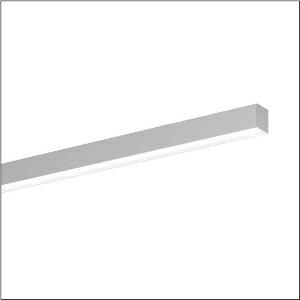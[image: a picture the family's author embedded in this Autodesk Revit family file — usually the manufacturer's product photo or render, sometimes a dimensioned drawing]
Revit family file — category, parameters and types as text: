
# Revit family: silica_r__21_51mx23tbt5s_3fb0
name_source: partatom
category: Lighting Fixtures
units: mm (PartAtom-declared; Revit-internal decimal feet)

## family parameters
Cut with Voids When Loaded = No
Host = Face
Light Source = No
Part Type = Normal
Room Calculation Point = No
Round Connector Dimension = Use Diameter
Shared = No

## types (1)
- --- (1 x LED, 4030 lm, 40.5 W, 6500K)
    Apparent Load = 41 VA
    CIE Flux Codes = 78 96 99 100 100
    Color Rendering = 80
    Color Temperature = 6500K
    Default Elevation = 1800 mm
    Description = Silica® 21, office luminaire, primary optical cover: prismatic diffuser, of PMMA, CAT 2 (L<= 3000cd/m²), light emission: direct distribution, primary light characteristic: symmetric, installation type: surface-mounted, LED, rated luminous flux: 4.030lm, luminous efficacy: 95lm/W, light colour: 8tw, colour temperature: 2700..6500K, control gear: ECG DALI, with terminal, 3+2-pole, max. 2.5mm², mains connection: 220..240V, AC, 50/60Hz, rated input power: 42.6W, luminaire housing, of aluminium, metallic grey (RAL 9006), length: 1.504mm, width: 53mm, height: 53mm, protection rating (complete): IP20, insulation class (complete): insulation class I (protective earthing), certification: CE, permissible operating ambient temperature: 0..+35°C, standard: EN 50419, packaging unit: 1 piece
    Height = 0 mm  [stored 0 ft]
    Lamp = 1 x LED
    Lamp Light Flux = 4030 lm
    Lamp Power = 40.5 W
    Lamp count = 1
    Length = 1504 mm
    Luminous efficacy = 100 lm/W
    Manufacturer = Siteco
    ModVariant = No
    Model = 51MX23TBT5S
    Mounting Place = Ceiling
    Mounting Type = Recessed
    Number of Poles = 1
    OnlyDefault = Yes
    Power Factor = 1
    Product Name = Silica® 21
    Product group = office luminaire | ceiling recessed
    ProductGroupID = 401
    Protection Class = Protection class I
    Protection Degree = IP 20
    RLX_Detail_Level = 1
    RLX_Emergency_Light_Flux = 0 lm
    RLX_Emergency_Type = 0
    RLX_Emergency_Type_DB = No
    RlxData = <blob elided: 18025 chars, md5=f705df25>
    Socket = socket
    Standby Power = 0 W
    System Light Flux = 4030 lm
    System Power = 41 W
    Type Comments = individual setting
    Type Image = l_1313588.jpg
    URL = http://relux.com
    VarID = @adj_089163
    Voltage = 0 V
    Weight = 0.00 kg
    Width = 53 mm

note: [stored X ft] marks values corroborated as IEEE doubles in the binary element streams (Revit-internal decimal feet)

## geometry (parser evidence)
native form markers: Blend x4, Sweep x11
no freeform markers — native parametric forms only
